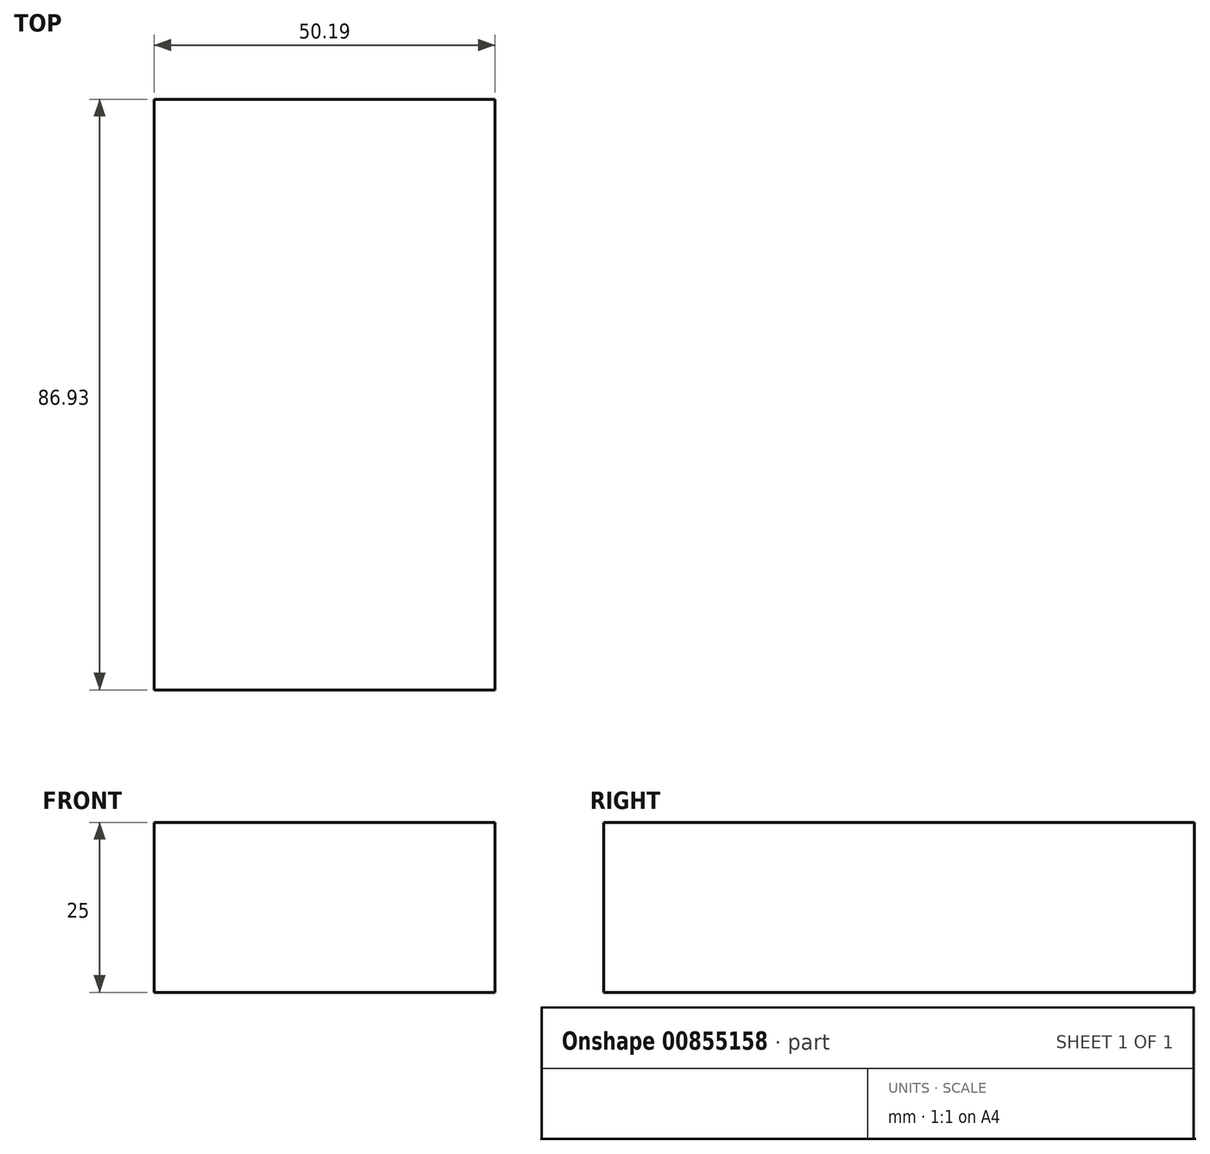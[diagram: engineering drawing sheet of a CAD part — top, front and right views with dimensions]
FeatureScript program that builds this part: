
annotation { "Feature Type Name" : "Feature", "Feature Type Description" : "" }
export const myFeature = defineFeature(function(context is Context, id is Id, definition is map)
    precondition{}
    {
        {
            var Q0;
            Q0=qCreatedBy(makeId("Top.planeOp"),FACE);
            var sketch = newSketch(context, id + "F0", { "sketchPlane" : qUnion([Q0])});
            skLineSegment(sketch, "E0.bottom", {"start": v(-33.1, 32.74) * mm, "end": v(-30.55, 32.74) * mm});
            skLineSegment(sketch, "E0.top", {"start": v(-33.1, 0) * mm, "end": v(-30.55, 0) * mm});
            skLineSegment(sketch, "E0.left", {"start": v(-33.1, 32.74) * mm, "end": v(-33.1, 0) * mm});
            skLineSegment(sketch, "E0.right", {"start": v(-30.55, 32.74) * mm, "end": v(-30.55, 0) * mm});
            skLineSegment(sketch, "E1.bottom", {"start": v(46.56, 202.96) * mm, "end": v(96.75, 202.96) * mm});
            skLineSegment(sketch, "E1.top", {"start": v(46.56, 289.9) * mm, "end": v(96.75, 289.9) * mm});
            skLineSegment(sketch, "E1.left", {"start": v(46.56, 202.96) * mm, "end": v(46.56, 289.9) * mm});
            skLineSegment(sketch, "E1.right", {"start": v(96.75, 202.96) * mm, "end": v(96.75, 289.9) * mm});
            skSolve(sketch);
        }
        {
            var Q0;
            Q0=makeQuery(id+"F0.imprint","IMPRINT",FACE,{"disambiguationData":[TD([[makeQuery(id+"F0.imprint","IMPRINT",EDGE,{"derivedFrom":sQuery(id+"F0.wireOp",EDGE,"E1.bottom")}),1.0]])]});
            extrude(context, id + "F1", {"entities" : qUnion([Q0]), "depth" : 25 * mm, "offsetDistance" : 25 * mm});
        }
    });
